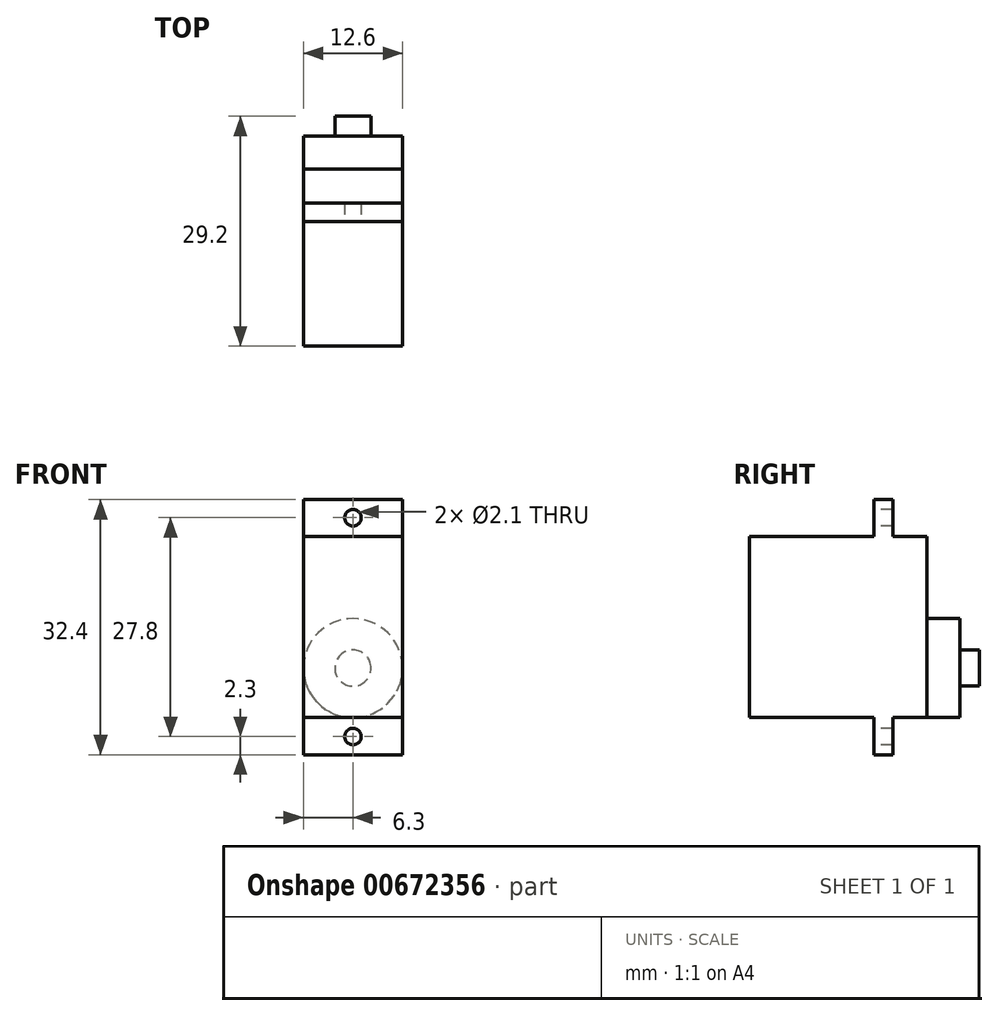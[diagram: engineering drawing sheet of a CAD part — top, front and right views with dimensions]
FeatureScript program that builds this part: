
annotation { "Feature Type Name" : "Feature", "Feature Type Description" : "" }
export const myFeature = defineFeature(function(context is Context, id is Id, definition is map)
    precondition{}
    {
        {
            var Q0;
            Q0=qCreatedBy(makeId("Front.planeOp"),FACE);
            var sketch = newSketch(context, id + "F0", { "sketchPlane" : qUnion([Q0])});
            skLineSegment(sketch, "E0.bottom", {"start": v(-6.3, 16.7) * mm, "end": v(6.3, 16.7) * mm});
            skLineSegment(sketch, "E0.top", {"start": v(-6.3, -6.3) * mm, "end": v(6.3, -6.3) * mm});
            skLineSegment(sketch, "E0.left", {"start": v(-6.3, 16.7) * mm, "end": v(-6.3, -6.3) * mm});
            skLineSegment(sketch, "E0.right", {"start": v(6.3, 16.7) * mm, "end": v(6.3, -6.3) * mm});
            skSolve(sketch);
        }
        {
            var Q0;
            Q0=makeQuery(id+"F0.imprint","IMPRINT",FACE,{"disambiguationData":[TD([[makeQuery(id+"F0.imprint","IMPRINT",EDGE,{"derivedFrom":sQuery(id+"F0.wireOp",EDGE,"E0.bottom")}),-1.0]])]});
            extrude(context, id + "F1", {"entities" : qUnion([Q0]), "depth" : 22.5 * mm, "offsetDistance" : 25 * mm});
        }
        {
            var Q0;
            Q0=makeQuery(id+"F1.opExtrude","CAP_FACE",FACE,{"disambiguationData":[OSD([sQuery(id+"F0.wireOp",EDGE,"E0.bottom"),sQuery(id+"F0.wireOp",EDGE,"E0.top"),sQuery(id+"F0.wireOp",EDGE,"E0.left"),sQuery(id+"F0.wireOp",EDGE,"E0.right")])],"isStart":false});
            cPlane(context, id + "F2", {"entities" : qUnion([Q0]), "cplaneType" : CPlaneType.OFFSET, "offset" : 15.8 * mm, "oppositeDirection" : true, "width" : 150 * mm, "height" : 150 * mm});
        }
        {
            var Q0;
            Q0=qCreatedBy(id+"F2.planeOp",FACE);
            var sketch = newSketch(context, id + "F3", { "sketchPlane" : qUnion([Q0])});
            skLineSegment(sketch, "E1.bottom", {"start": v(-6.3, 21.4) * mm, "end": v(6.3, 21.4) * mm});
            skLineSegment(sketch, "E1.top", {"start": v(-6.3, -11) * mm, "end": v(6.3, -11) * mm});
            skLineSegment(sketch, "E1.left", {"start": v(-6.3, 21.4) * mm, "end": v(-6.3, -11) * mm});
            skLineSegment(sketch, "E1.right", {"start": v(6.3, 21.4) * mm, "end": v(6.3, -11) * mm});
            skSolve(sketch);
        }
        {
            var Q0;
            Q0 = qSketchRegion(id + "F3", true);
            extrude(context, id + "F4", {"entities" : qUnion([Q0]), "operationType" : NewBodyOperationType.ADD, "oppositeDirection" : true, "depth" : 2.4 * mm, "offsetDistance" : 25 * mm});
        }
        {
            var Q0;
            Q0=qCreatedBy(id+"F2.planeOp",FACE);
            var sketch = newSketch(context, id + "F5", { "sketchPlane" : qUnion([Q0])});
            skCircle(sketch, "E2", {"center": v(0, 19.1) * mm, "radius": 1.05 * mm});
            skCircle(sketch, "E3", {"center": v(0, -8.7) * mm, "radius": 1.05 * mm});
            skSolve(sketch);
        }
        {
            var Q0;
            Q0 = qSketchRegion(id + "F5", true);
            extrude(context, id + "F6", {"entities" : qUnion([Q0]), "operationType" : NewBodyOperationType.REMOVE, "oppositeDirection" : true, "depth" : 25 * mm, "offsetDistance" : 25 * mm});
        }
        {
            var Q0;
            Q0=qCreatedBy(makeId("Front.planeOp"),FACE);
            var sketch = newSketch(context, id + "F7", { "sketchPlane" : qUnion([Q0])});
            skCircle(sketch, "E4", {"center": v(0, 0) * mm, "radius": 6.3 * mm});
            skSolve(sketch);
        }
        {
            var Q0;
            Q0 = qSketchRegion(id + "F7", true);
            extrude(context, id + "F8", {"entities" : qUnion([Q0]), "operationType" : NewBodyOperationType.ADD, "oppositeDirection" : true, "depth" : 4.2 * mm, "offsetDistance" : 25 * mm});
        }
        {
            var Q0;
            Q0=qCreatedBy(makeId("Front.planeOp"),FACE);
            var sketch = newSketch(context, id + "F9", { "sketchPlane" : qUnion([Q0])});
            skCircle(sketch, "E5", {"center": v(0, 0) * mm, "radius": 2.3 * mm});
            skSolve(sketch);
        }
        {
            var Q0;
            Q0 = qSketchRegion(id + "F9", true);
            extrude(context, id + "F10", {"entities" : qUnion([Q0]), "operationType" : NewBodyOperationType.ADD, "oppositeDirection" : true, "depth" : 6.7 * mm, "offsetDistance" : 25 * mm});
        }
    });
